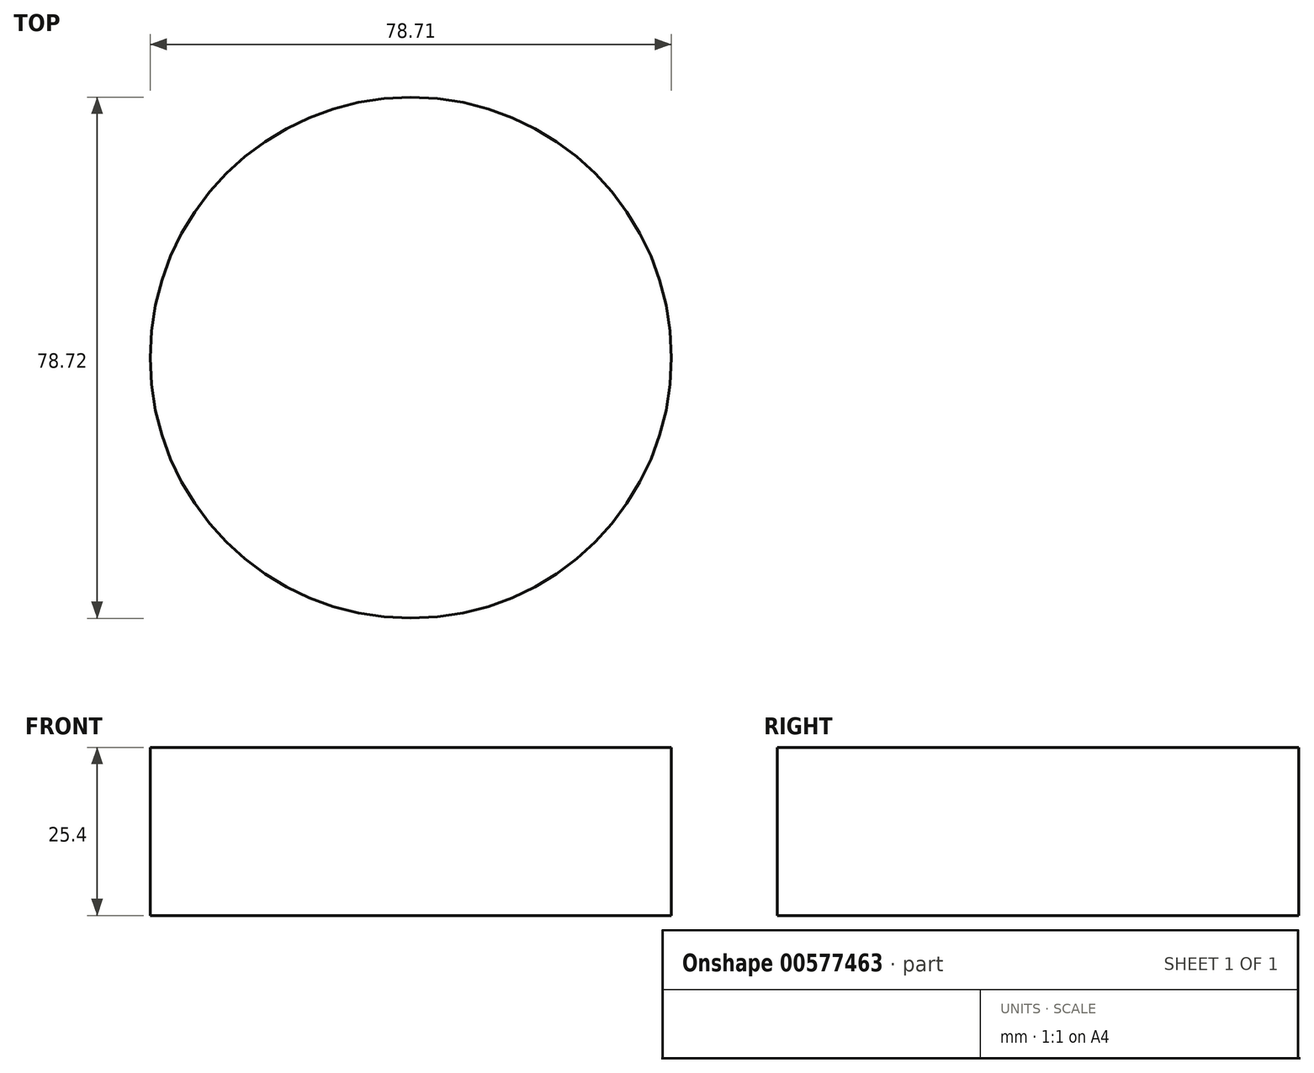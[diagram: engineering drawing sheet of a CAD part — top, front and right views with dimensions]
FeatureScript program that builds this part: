
annotation { "Feature Type Name" : "Feature", "Feature Type Description" : "" }
export const myFeature = defineFeature(function(context is Context, id is Id, definition is map)
    precondition{}
    {
        {
            var Q0;
            Q0=qCreatedBy(makeId("Top.planeOp"),FACE);
            var sketch = newSketch(context, id + "F0", { "sketchPlane" : qUnion([Q0])});
            skCircle(sketch, "E0", {"center": v(44.6, 0) * mm, "radius": 39.36 * mm});
            skSolve(sketch);
        }
        {
            var Q0;
            Q0 = qSketchRegion(id + "F0", true);
            extrude(context, id + "F1", {"entities" : qUnion([Q0]), "oppositeDirection" : true, "depth" : 25.4 * mm, "offsetDistance" : 25.4 * mm});
        }
    });
